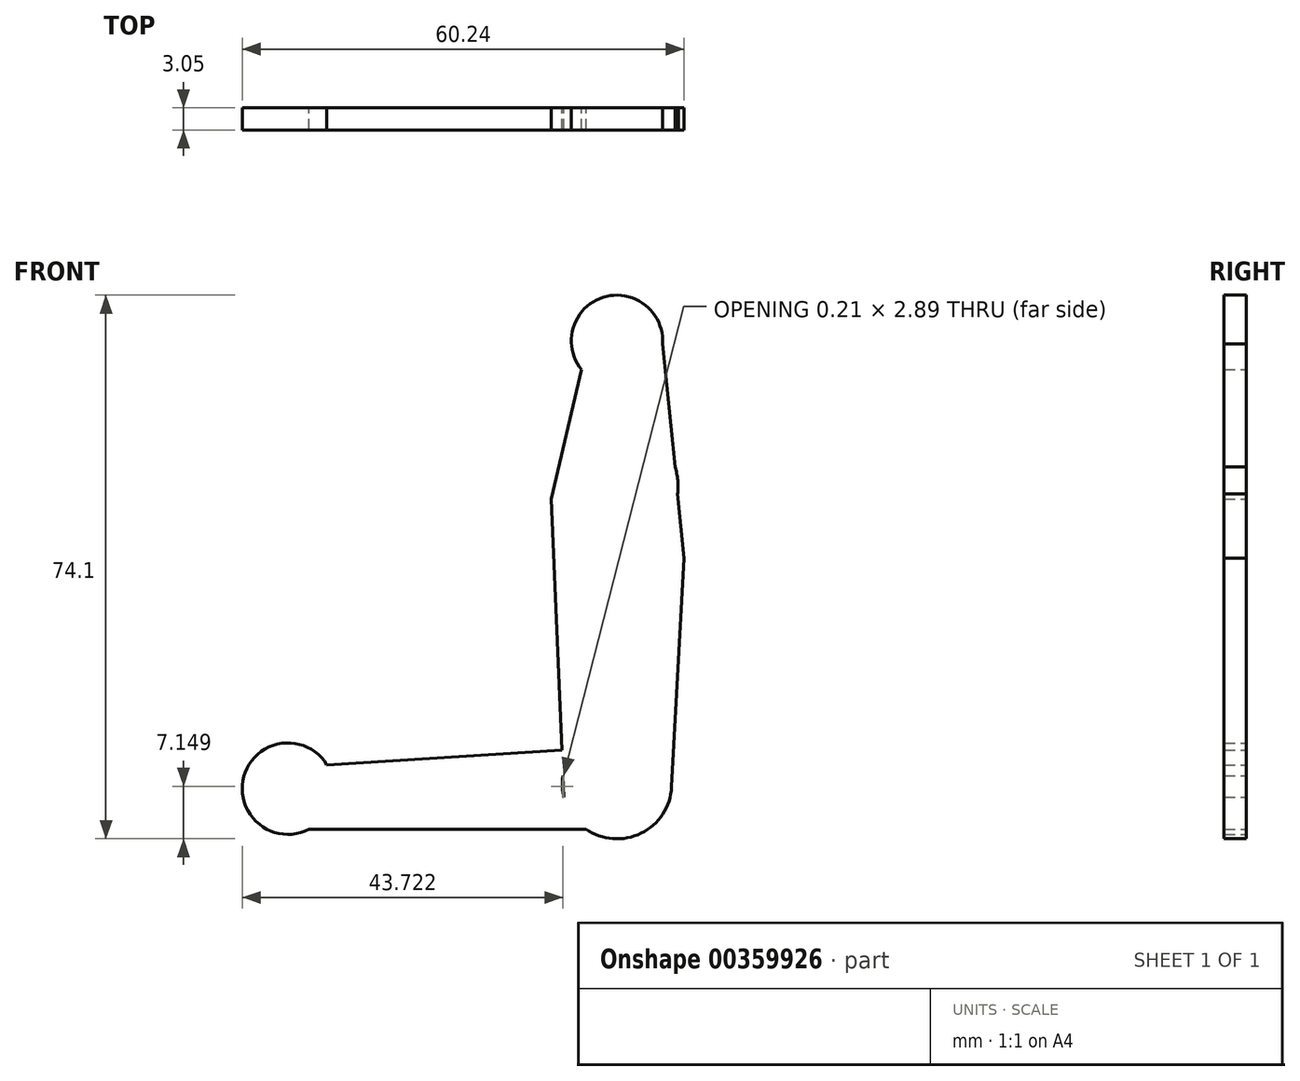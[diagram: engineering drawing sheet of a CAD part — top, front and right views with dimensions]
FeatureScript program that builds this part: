
annotation { "Feature Type Name" : "Feature", "Feature Type Description" : "" }
export const myFeature = defineFeature(function(context is Context, id is Id, definition is map)
    precondition{}
    {
        {
            var Q0;
            Q0=qCreatedBy(makeId("Front.planeOp"),FACE);
            var sketch = newSketch(context, id + "F0", { "sketchPlane" : qUnion([Q0])});
            skCircle(sketch, "E0", {"center": v(0, 65.38) * mm, "radius": 6.22 * mm});
            skCircle(sketch, "E1", {"center": v(0, 45.53) * mm, "radius": 8.35 * mm});
            skCircle(sketch, "E2", {"center": v(0, 4.96) * mm, "radius": 7.46 * mm});
            skCircle(sketch, "E3", {"center": v(-44.85, 4.34) * mm, "radius": 6.23 * mm});
            skLineSegment(sketch, "E4", {"start": v(0, 59.16) * mm, "end": v(0, 12.42) * mm});
            skLineSegment(sketch, "E5", {"start": v(-7.25, 3.2) * mm, "end": v(-38.72, 3.2) * mm});
            skLineSegment(sketch, "E6", {"start": v(6.2, 64.96) * mm, "end": v(9.16, 35.77) * mm});
            skLineSegment(sketch, "E7", {"start": v(-4.82, 61.45) * mm, "end": v(-8.98, 43.83) * mm});
            skLineSegment(sketch, "E8", {"start": v(-8.98, 43.83) * mm, "end": v(-7.25, 3.2) * mm});
            skLineSegment(sketch, "E9", {"start": v(9.16, 35.77) * mm, "end": v(7.45, 4.55) * mm});
            skLineSegment(sketch, "E10", {"start": v(-5.78, 9.68) * mm, "end": v(-39.53, 7.59) * mm});
            skLineSegment(sketch, "E11", {"start": v(-4.23, -1.19) * mm, "end": v(-41.97, -1.19) * mm});
            skSolve(sketch);
        }
        {
            var Q0;
            Q0 = qSketchRegion(id + "F0", true);
            extrude(context, id + "F1", {"entities" : qUnion([Q0]), "depth" : 3.05 * mm});
        }
    });
